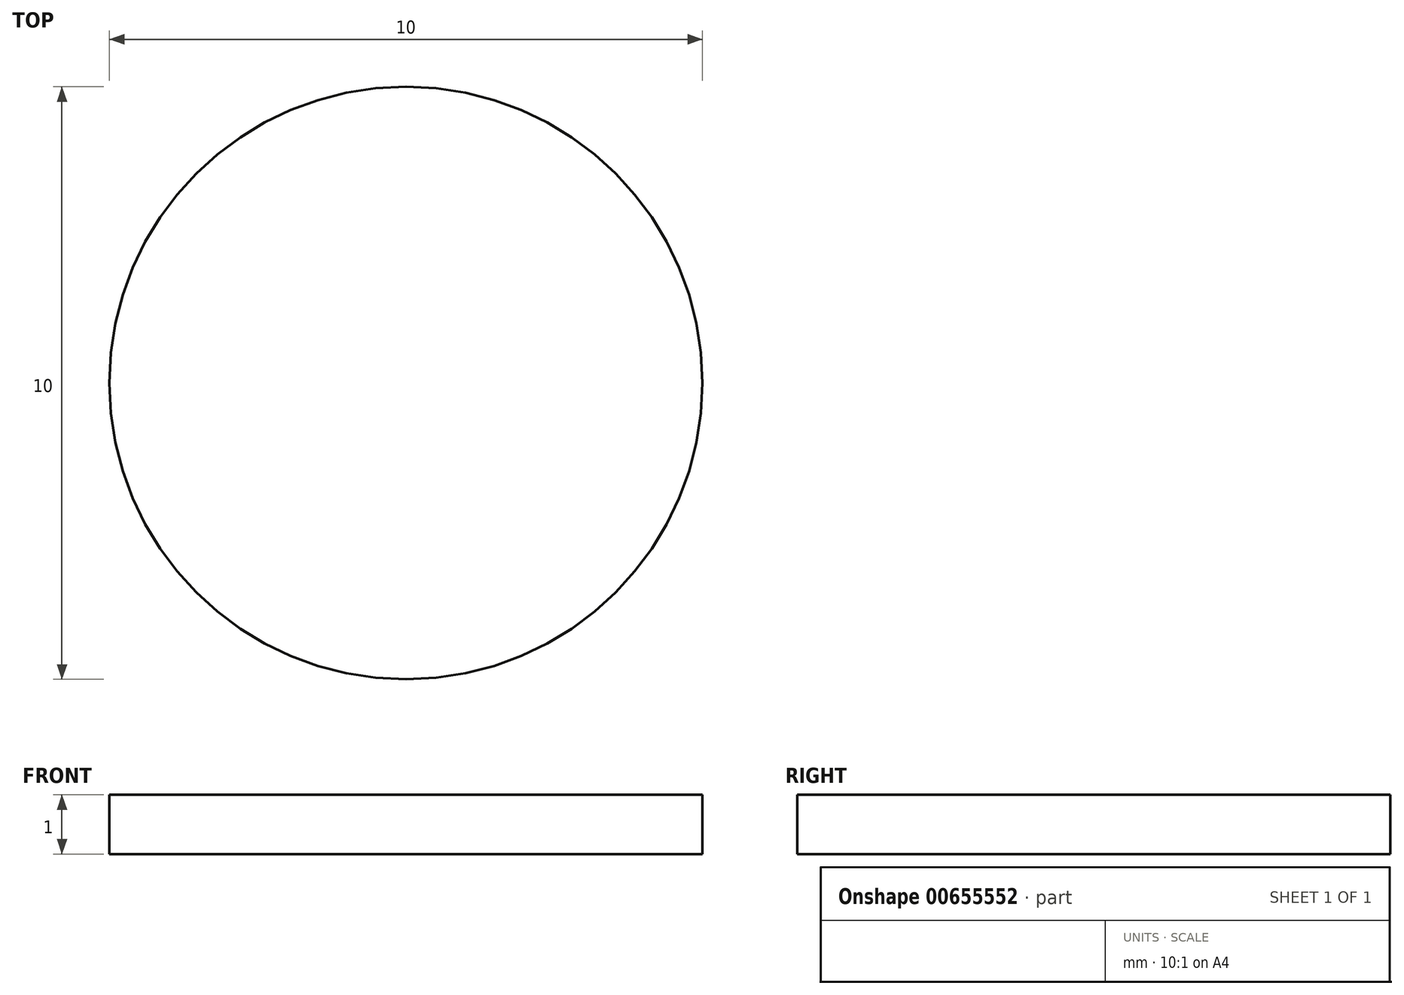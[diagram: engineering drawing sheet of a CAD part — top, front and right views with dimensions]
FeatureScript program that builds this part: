
annotation { "Feature Type Name" : "Feature", "Feature Type Description" : "" }
export const myFeature = defineFeature(function(context is Context, id is Id, definition is map)
    precondition{}
    {
        {
            var Q0;
            Q0=qCreatedBy(makeId("Top.planeOp"),FACE);
            var sketch = newSketch(context, id + "F0", { "sketchPlane" : qUnion([Q0])});
            skCircle(sketch, "E0", {"center": v(0, 0) * mm, "radius": 5 * mm});
            skSolve(sketch);
        }
        {
            var Q0;
            Q0 = qSketchRegion(id + "F0", true);
            extrude(context, id + "F1", {"entities" : qUnion([Q0]), "depth" : 1 * mm, "offsetDistance" : 25 * mm});
        }
    });
